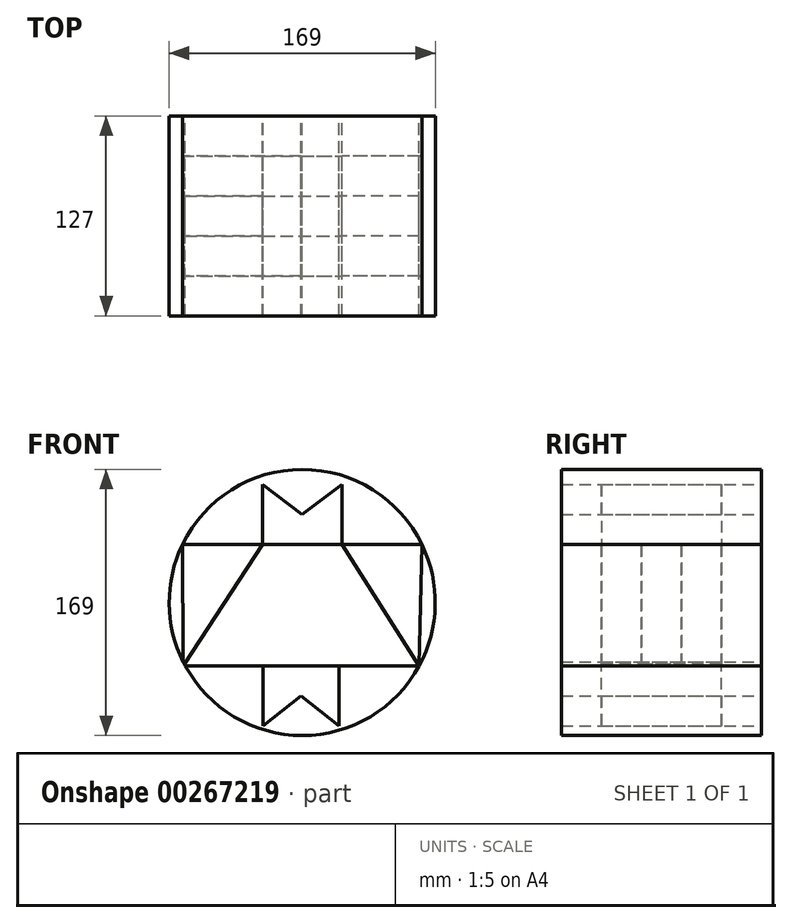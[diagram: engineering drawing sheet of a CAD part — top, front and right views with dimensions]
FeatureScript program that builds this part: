
annotation { "Feature Type Name" : "Feature", "Feature Type Description" : "" }
export const myFeature = defineFeature(function(context is Context, id is Id, definition is map)
    precondition{}
    {
        {
            var Q0;
            Q0=qCreatedBy(makeId("Front.planeOp"),FACE);
            var sketch = newSketch(context, id + "F0", { "sketchPlane" : qUnion([Q0])});
            skLineSegment(sketch, "E0.bottom", {"start": v(76.05, 76.14) * mm, "end": v(25.25, 76.14) * mm});
            skLineSegment(sketch, "E0.top", {"start": v(76.05, 38.04) * mm, "end": v(25.25, 38.04) * mm});
            skLineSegment(sketch, "E0.left", {"start": v(76.05, 76.14) * mm, "end": v(76.05, 38.04) * mm});
            skLineSegment(sketch, "E0.right", {"start": v(25.25, 76.14) * mm, "end": v(25.25, 38.04) * mm});
            skLineSegment(sketch, "E1.bottom", {"start": v(-76.07, 76.09) * mm, "end": v(-25.27, 76.09) * mm});
            skLineSegment(sketch, "E1.top", {"start": v(-76.07, 37.99) * mm, "end": v(-25.27, 37.99) * mm});
            skLineSegment(sketch, "E1.left", {"start": v(-76.07, 76.09) * mm, "end": v(-76.07, 37.99) * mm});
            skLineSegment(sketch, "E1.right", {"start": v(-25.27, 76.09) * mm, "end": v(-25.27, 37.99) * mm});
            skLineSegment(sketch, "E2.bottom", {"start": v(-75.58, -77.12) * mm, "end": v(-24.78, -77.12) * mm});
            skLineSegment(sketch, "E2.top", {"start": v(-75.58, -39.02) * mm, "end": v(-24.78, -39.02) * mm});
            skLineSegment(sketch, "E2.left", {"start": v(-75.58, -77.12) * mm, "end": v(-75.58, -39.02) * mm});
            skLineSegment(sketch, "E2.right", {"start": v(-24.78, -77.12) * mm, "end": v(-24.78, -39.02) * mm});
            skLineSegment(sketch, "E3", {"start": v(-24.78, -39.02) * mm, "end": v(25.25, 38.04) * mm});
            skLineSegment(sketch, "E4", {"start": v(-25.27, 37.99) * mm, "end": v(-75.58, -39.02) * mm});
            skLineSegment(sketch, "E5.bottom", {"start": v(74.32, -77.12) * mm, "end": v(23.52, -77.12) * mm});
            skLineSegment(sketch, "E5.top", {"start": v(74.32, -39.02) * mm, "end": v(23.52, -39.02) * mm});
            skLineSegment(sketch, "E5.left", {"start": v(74.32, -77.12) * mm, "end": v(74.32, -39.02) * mm});
            skLineSegment(sketch, "E5.right", {"start": v(23.52, -77.12) * mm, "end": v(23.52, -39.02) * mm});
            skLineSegment(sketch, "E6", {"start": v(74.32, -39.02) * mm, "end": v(25.25, 38.04) * mm});
            skLineSegment(sketch, "E7", {"start": v(23.52, -39.02) * mm, "end": v(-25.27, 37.99) * mm});
            skLineSegment(sketch, "E8", {"start": v(74.32, -39.02) * mm, "end": v(76.05, 38.04) * mm});
            skLineSegment(sketch, "E9", {"start": v(-76.07, 37.99) * mm, "end": v(-75.58, -39.02) * mm});
            skLineSegment(sketch, "E10", {"start": v(-24.78, -39.02) * mm, "end": v(23.52, -39.02) * mm});
            skLineSegment(sketch, "E11", {"start": v(-25.27, 37.99) * mm, "end": v(25.25, 38.04) * mm});
            skLineSegment(sketch, "E12", {"start": v(-24.78, -39.02) * mm, "end": v(23.52, -77.12) * mm});
            skLineSegment(sketch, "E13", {"start": v(23.52, -39.02) * mm, "end": v(-24.78, -77.12) * mm});
            skLineSegment(sketch, "E14", {"start": v(-25.27, 76.09) * mm, "end": v(25.25, 38.04) * mm});
            skLineSegment(sketch, "E15", {"start": v(-25.27, 37.99) * mm, "end": v(25.25, 76.14) * mm});
            skCircle(sketch, "E16", {"center": v(0, 1.2) * mm, "radius": 84.5 * mm});
            skSolve(sketch);
        }
        {
            var Q0;
            {var subQ0=sQuery(id+"F0.wireOp",EDGE,"E8");Q0=makeQuery(id+"F0.imprint","IMPRINT",FACE,{"disambiguationData":[TD([[makeQuery(id+"F0.imprint","IMPRINT",EDGE,{"derivedFrom":subQ0}),-1.0]])]});}
            var Q1;
            {var subQ4=sQuery(id+"F0.wireOp",EDGE,"E0.top");Q1=makeQuery(id+"F0.imprint","IMPRINT",FACE,{"disambiguationData":[TD([[makeQuery(id+"F0.imprint","IMPRINT",EDGE,{"derivedFrom":subQ4}),-1.0]])]});}
            var Q2;
            {var subQ1=sQuery(id+"F0.wireOp",EDGE,"E0.bottom");var subQ7=sQuery(id+"F0.wireOp",EDGE,"E16");var subQ9=makeQuery(id+"F0.imprint","INTERSECT",VERTEX,{"derivedFrom":[subQ1,subQ7]});Q2=makeQuery(id+"F0.imprint","IMPRINT",FACE,{"disambiguationData":[TD([[makeQuery(id+"F0.imprint","IMPRINT",EDGE,{"disambiguationData":[TD([[subQ9,-1.0]])],"derivedFrom":subQ7}),1.0]])]});}
            var Q3;
            {var subQ4=sQuery(id+"F0.wireOp",EDGE,"E1.top");Q3=makeQuery(id+"F0.imprint","IMPRINT",FACE,{"disambiguationData":[TD([[makeQuery(id+"F0.imprint","IMPRINT",EDGE,{"derivedFrom":subQ4}),1.0]])]});}
            var Q4;
            {var subQ0=sQuery(id+"F0.wireOp",EDGE,"E16");var subQ1=sQuery(id+"F0.wireOp",EDGE,"E9");var subQ3=makeQuery(id+"F0.imprint","INTERSECT",VERTEX,{"derivedFrom":[subQ1,subQ0]});Q4=makeQuery(id+"F0.imprint","IMPRINT",FACE,{"disambiguationData":[TD([[makeQuery(id+"F0.imprint","IMPRINT",EDGE,{"disambiguationData":[TD([[subQ3,1.0]])],"derivedFrom":subQ1}),-1.0]])]});}
            var Q5;
            {var subQ0=sQuery(id+"F0.wireOp",EDGE,"E2.right");Q5=makeQuery(id+"F0.imprint","IMPRINT",FACE,{"disambiguationData":[TD([[makeQuery(id+"F0.imprint","IMPRINT",EDGE,{"derivedFrom":subQ0}),1.0]])]});}
            var Q6;
            {var subQ1=sQuery(id+"F0.wireOp",EDGE,"E2.bottom");var subQ7=sQuery(id+"F0.wireOp",EDGE,"E16");var subQ8=makeQuery(id+"F0.imprint","INTERSECT",VERTEX,{"derivedFrom":[subQ1,subQ7]});Q6=makeQuery(id+"F0.imprint","IMPRINT",FACE,{"disambiguationData":[TD([[makeQuery(id+"F0.imprint","IMPRINT",EDGE,{"disambiguationData":[TD([[subQ8,-1.0]])],"derivedFrom":subQ7}),1.0]])]});}
            var Q7;
            {var subQ4=sQuery(id+"F0.wireOp",EDGE,"E5.top");Q7=makeQuery(id+"F0.imprint","IMPRINT",FACE,{"disambiguationData":[TD([[makeQuery(id+"F0.imprint","IMPRINT",EDGE,{"derivedFrom":subQ4}),1.0]])]});}
            extrude(context, id + "F1", {"entities" : qUnion([Q0, Q1, Q2, Q3, Q4, Q5, Q6, Q7]), "endBound" : BoundingType.SYMMETRIC, "depth" : 127 * mm});
        }
        {
            var Q0;
            {var subQ0=sQuery(id+"F0.wireOp",EDGE,"E11");Q0=makeQuery(id+"F0.imprint","IMPRINT",FACE,{"disambiguationData":[TD([[makeQuery(id+"F0.imprint","IMPRINT",EDGE,{"derivedFrom":subQ0}),-1.0]])]});}
            var Q1;
            {var subQ3=sQuery(id+"F0.wireOp",EDGE,"E16");var subQ6=sQuery(id+"F0.wireOp",EDGE,"E2.top");var subQ9=makeQuery(id+"F0.imprint","INTERSECT",VERTEX,{"derivedFrom":[subQ6,subQ3]});Q1=makeQuery(id+"F0.imprint","IMPRINT",FACE,{"disambiguationData":[TD([[makeQuery(id+"F0.imprint","IMPRINT",EDGE,{"disambiguationData":[TD([[subQ9,1.0]])],"derivedFrom":subQ3}),1.0]])]});}
            var Q2;
            {var subQ4=sQuery(id+"F0.wireOp",EDGE,"E5.top");Q2=makeQuery(id+"F0.imprint","IMPRINT",FACE,{"disambiguationData":[TD([[makeQuery(id+"F0.imprint","IMPRINT",EDGE,{"derivedFrom":subQ4}),-1.0]])]});}
            var Q3;
            {var subQ0=sQuery(id+"F0.wireOp",EDGE,"E10");Q3=makeQuery(id+"F0.imprint","IMPRINT",FACE,{"disambiguationData":[TD([[makeQuery(id+"F0.imprint","IMPRINT",EDGE,{"derivedFrom":subQ0}),1.0]])]});}
            extrude(context, id + "F2", {"entities" : qUnion([Q0, Q1, Q2, Q3]), "endBound" : BoundingType.SYMMETRIC, "depth" : 25.4 * mm});
        }
        {
            var Q0;
            Q0=makeQuery(id+"F0.imprint","IMPRINT",FACE,{"disambiguationData":[TD([[makeQuery(id+"F0.imprint","IMPRINT",EDGE,{"derivedFrom":sQuery(id+"F0.wireOp",EDGE,"E0.top")}),1.0]])]});
            var Q1;
            {var subQ0=sQuery(id+"F0.wireOp",EDGE,"E11");Q1=makeQuery(id+"F0.imprint","IMPRINT",FACE,{"disambiguationData":[TD([[makeQuery(id+"F0.imprint","IMPRINT",EDGE,{"derivedFrom":subQ0}),1.0]])]});}
            var Q2;
            {var subQ0=sQuery(id+"F0.wireOp",EDGE,"E1.top");Q2=makeQuery(id+"F0.imprint","IMPRINT",FACE,{"disambiguationData":[TD([[makeQuery(id+"F0.imprint","IMPRINT",EDGE,{"derivedFrom":subQ0}),-1.0]])]});}
            var Q3;
            {var subQ0=sQuery(id+"F0.wireOp",EDGE,"E2.right");Q3=makeQuery(id+"F0.imprint","IMPRINT",FACE,{"disambiguationData":[TD([[makeQuery(id+"F0.imprint","IMPRINT",EDGE,{"derivedFrom":subQ0}),-1.0]])]});}
            var Q4;
            {var subQ0=sQuery(id+"F0.wireOp",EDGE,"E5.right");Q4=makeQuery(id+"F0.imprint","IMPRINT",FACE,{"disambiguationData":[TD([[makeQuery(id+"F0.imprint","IMPRINT",EDGE,{"derivedFrom":subQ0}),1.0]])]});}
            var Q5;
            {var subQ0=sQuery(id+"F0.wireOp",EDGE,"E10");Q5=makeQuery(id+"F0.imprint","IMPRINT",FACE,{"disambiguationData":[TD([[makeQuery(id+"F0.imprint","IMPRINT",EDGE,{"derivedFrom":subQ0}),-1.0]])]});}
            var Q6;
            {var subQ0=sQuery(id+"F0.wireOp",EDGE,"E0.right");Q6=makeQuery(id+"F0.imprint","IMPRINT",FACE,{"disambiguationData":[TD([[makeQuery(id+"F0.imprint","IMPRINT",EDGE,{"derivedFrom":subQ0}),-1.0]])]});}
            var Q7;
            {var subQ0=sQuery(id+"F0.wireOp",EDGE,"E1.right");Q7=makeQuery(id+"F0.imprint","IMPRINT",FACE,{"disambiguationData":[TD([[makeQuery(id+"F0.imprint","IMPRINT",EDGE,{"derivedFrom":subQ0}),1.0]])]});}
            extrude(context, id + "F3", {"entities" : qUnion([Q0, Q1, Q2, Q3, Q4, Q5, Q6, Q7]), "endBound" : BoundingType.SYMMETRIC, "depth" : 76.2 * mm});
        }
    });
